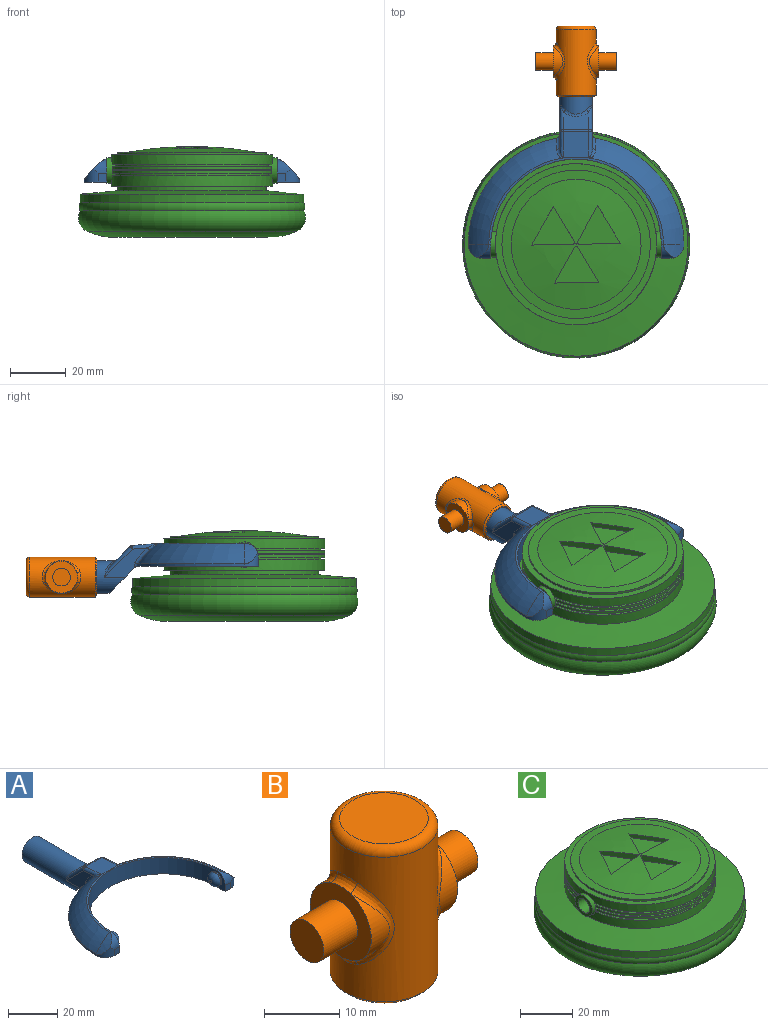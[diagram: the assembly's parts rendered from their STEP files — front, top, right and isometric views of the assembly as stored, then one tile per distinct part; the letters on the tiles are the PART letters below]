
ASSEMBLY  parts=3 mates=2
PART A: 48 faces, bbox 77.3x80.8x18.2 mm
  f0: plane 11.99x9.83mm, normal (0,-0.71,-0.71), area 141.5mm2, adj f1,f2,f9,f30,f43,f46
  f1: plane 15.39x10.49mm, normal (-1,0,0), area 63.5mm2, adj f0,f30,f32,f36,f46,f47
  f2: plane 15.39x10.49mm, normal (1,0,0), area 63.5mm2, adj f0,f30,f34,f39,f43,f44
  f3: plane 9.14x6.37mm, normal (0,0.71,0.71), area 67.6mm2, adj f35,f36,f39,f40
  f4: cylinder r=38.61mm len=37.99mm, axis (0,0,-1), area 42.6mm2, adj f6,f9,f17,f46,f47
  f5: torus R=19.3mm, axis (0,0,-1), area 507.8mm2, adj f10,f11,f12,f29,f42,f44
  f6: torus R=19.3mm, axis (0,0,-1), area 507.8mm2, adj f4,f11,f15,f28,f45,f47
  f7: cylinder r=30.48mm len=60.96mm, axis (0,0,-1), area 746.6mm2, adj f8,f9,f11,f14,f21,f24
  f8: plane 8.13x5.08mm, normal (-1,0,0), area 19.9mm2, adj f7,f9,f13,f19,f24
  f9: plane 77.22x43.73mm, normal (0,0,-1), area 956.2mm2, adj f0,f4,f7,f8,f10,f13,f14,f16
  f10: cylinder r=38.61mm len=37.99mm, axis (0,0,-1), area 42.6mm2, adj f5,f9,f20,f43,f44
  f11: plane 62.55x30.95mm, normal (0,0,1), area 75mm2, adj f5,f6,f7,f18,f19,f27
  f12: cylinder r=22.71mm len=7.33mm, axis (0,1,0), area 24.8mm2, adj f5,f19,f20
  f13: plane 3.05x3.05mm, normal (0,-1,0), area 9.3mm2, adj f8,f9,f19,f20
  f14: plane 8.13x5.08mm, normal (1,0,0), area 19.9mm2, adj f7,f9,f16,f18,f21
  f15: cylinder r=22.71mm len=7.33mm, axis (0,1,0), area 24.8mm2, adj f6,f17,f18
  f16: plane 3.05x3.05mm, normal (0,-1,0), area 9.3mm2, adj f9,f14,f17,f18
  f17: cylinder r=5.08mm len=5.08mm, axis (0,0,-1), area 21.9mm2, adj f4,f9,f15,f16,f18
  f18: cylinder r=5.08mm len=5.08mm, axis (-1,0,0), area 21.9mm2, adj f11,f14,f15,f16,f17
  f19: cylinder r=5.08mm len=5.08mm, axis (-1,0,0), area 21.9mm2, adj f8,f11,f12,f13,f20
  f20: cylinder r=5.08mm len=5.08mm, axis (0,0,-1), area 21.9mm2, adj f9,f10,f12,f13,f19
  f21: cylinder r=3.17mm len=6.35mm, axis (-1,0,0), area 12.7mm2, adj f7,f14,f23
  f22: plane 1.27x1.27mm, normal (1,0,0), area 1.3mm2, adj f23
  f23: torus R=0.64mm, axis (1,0,0), area 56.5mm2, adj f21,f22
  f24: cylinder r=3.17mm len=6.35mm, axis (1,0,0), area 12.7mm2, adj f7,f8,f26
  f25: plane 1.27x1.27mm, normal (-1,0,0), area 1.3mm2, adj f26
  f26: torus R=0.64mm, axis (-1,0,0), area 56.5mm2, adj f24,f25
  f27: plane 9.86x9.36mm, normal (0,0.09,1), area 85.6mm2, adj f11,f28,f29,f32,f34,f35,f42,f45
  f28: plane 1.04x0.17mm, normal (0,-1,0), area 0mm2, adj f6,f27,f45
  f29: plane 1.04x0.17mm, normal (0,-1,0), area 0mm2, adj f5,f27,f42
  f30: cylinder r=5.84mm len=33.01mm, axis (0,-1,0), area 1029.7mm2, adj f0,f1,f2,f31,f38,f40,f41
  f31: plane 11.68x11.68mm, normal (0,1,0), area 107.2mm2, adj f30
  f32: cylinder r=1.27mm len=9.13mm, axis (0,-1,0.09), area 14.4mm2, adj f1,f27,f33,f45
  f33: sphere r=1.27mm, area 1.5mm2, adj f32,f35,f36
  f34: cylinder r=1.27mm len=9.13mm, axis (0,1,-0.09), area 14.4mm2, adj f2,f27,f37,f42
  f35: cylinder r=1.27mm len=9.14mm, axis (-1,0,0), area 8.1mm2, adj f3,f27,f33,f37
  f36: cylinder r=1.27mm len=10.91mm, axis (0,-0.71,0.71), area 23.1mm2, adj f1,f3,f33,f38
  f37: sphere r=1.27mm, area 1.5mm2, adj f34,f35,f39
  f38: bspline ~4.55x2.75mm, area 2.3mm2, adj f30,f36,f40
  f39: cylinder r=1.27mm len=10.91mm, axis (0,0.71,-0.71), area 23.1mm2, adj f2,f3,f37,f41
  f40: bspline ~9.14x2.56mm, area 10.7mm2, adj f3,f30,f38,f41
  f41: bspline ~5.23x3.53mm, area 2.3mm2, adj f30,f39,f40
  f42: bspline ~4.62x3.14mm, area 5.2mm2, adj f5,f27,f29,f34,f44
  f43: cylinder r=1.27mm len=1.74mm, axis (0,0,-1), area 1.9mm2, adj f0,f2,f9,f10,f44
  f44: bspline ~8.6x7.86mm, area 11.9mm2, adj f2,f5,f10,f42,f43
  f45: bspline ~4.62x3.14mm, area 5.2mm2, adj f6,f27,f28,f32,f47
  f46: cylinder r=1.27mm len=1.74mm, axis (0,0,-1), area 1.9mm2, adj f0,f1,f4,f9,f47
  f47: bspline ~8.6x7.86mm, area 11.9mm2, adj f1,f4,f6,f45,f46
PART B: 25 faces, bbox 28.9x15.5x25.4 mm
  f0: cylinder r=5.71mm len=10.81mm, axis (-1,0,0), area 26.2mm2, adj f5,f15
  f1: cylinder r=5.71mm len=10.81mm, axis (-1,0,0), area 26.2mm2, adj f8,f11
  f2: cylinder r=7.14mm len=23.5mm, axis (0,0,-1), area 763.2mm2, adj f9,f10,f11,f12,f13,f14,f15,f16
  f3: plane 11.75x11.75mm, normal (0,0,1), area 108.4mm2, adj f17
  f4: plane 13.02x13.02mm, normal (0,0,-1), area 16.3mm2, adj f22,f24
  f5: plane 11.46x11.46mm, normal (1,0,0), area 70.9mm2, adj f0,f6,f13,f16,f18
  f6: cylinder r=5.71mm len=10.81mm, axis (-1,0,0), area 26.2mm2, adj f5,f14
  f7: cylinder r=5.71mm len=10.81mm, axis (-1,0,0), area 26.2mm2, adj f8,f10
  f8: plane 11.46x11.46mm, normal (-1,0,0), area 70.9mm2, adj f1,f7,f9,f12,f20
  f9: bspline ~4.64x1.73mm, area 6.5mm2, adj f2,f8,f10,f11
  f10: bspline ~13.62x4.91mm, area 20.7mm2, adj f2,f7,f9,f12
  f11: bspline ~13.6x4.87mm, area 20.7mm2, adj f1,f2,f9,f12
  f12: bspline ~4.64x1.73mm, area 6.5mm2, adj f2,f8,f10,f11
  f13: bspline ~4.64x1.73mm, area 6.5mm2, adj f2,f5,f14,f15
  f14: bspline ~13.62x4.91mm, area 20.7mm2, adj f2,f6,f13,f16
  f15: bspline ~13.6x4.87mm, area 20.7mm2, adj f0,f2,f13,f16
  f16: bspline ~4.64x1.73mm, area 6.5mm2, adj f2,f5,f14,f15
  f17: torus R=5.87mm, axis (0,0,1), area 83.8mm2, adj f2,f3
  f18: cylinder r=3.17mm len=6.35mm, axis (-1,0,0), area 126.7mm2, adj f5,f19
  f19: plane 6.35x6.35mm, normal (1,0,0), area 31.7mm2, adj f18
  f20: cylinder r=3.17mm len=6.35mm, axis (1,0,0), area 126.7mm2, adj f8,f21
  f21: plane 6.35x6.35mm, normal (-1,0,0), area 31.7mm2, adj f20
  f22: cylinder r=6.1mm len=22.86mm, axis (0,0,-1), area 875.6mm2, adj f4,f23
  f23: plane 12.19x12.19mm, normal (0,0,-1), area 116.7mm2, adj f22
  f24: cone r=7.14mm half-angle=45deg, axis (0,0,1), area 38.5mm2, adj f2,f4
PART C: 57 faces, bbox 96.3x96.3x32.5 mm
  f0: cylinder r=28.87mm len=57.73mm, axis (0,0,-1), area 676.7mm2, adj f1,f2,f33,f53,f54
  f1: plane 57.11x24.62mm, normal (0,0,1), area 101.3mm2, adj f0,f3,f53,f54
  f2: plane 57.11x24.62mm, normal (0,0,1), area 101.3mm2, adj f0,f4,f53,f54
  f3: cylinder r=27.6mm len=54.55mm, axis (0,0,-1), area 49.5mm2, adj f1,f6,f53,f54
  f4: cylinder r=27.6mm len=54.55mm, axis (0,0,-1), area 49.5mm2, adj f2,f5,f53,f54
  f5: plane 57.04x24.42mm, normal (0,0,-1), area 100.8mm2, adj f4,f8,f53,f54
  f6: plane 57.04x24.42mm, normal (0,0,-1), area 100.8mm2, adj f3,f7,f53,f54
  f7: cylinder r=28.87mm len=57.04mm, axis (0,0,-1), area 77.8mm2, adj f6,f10,f53,f54
  f8: cylinder r=28.87mm len=57.04mm, axis (0,0,-1), area 77.8mm2, adj f5,f9,f53,f54
  f9: plane 57.01x24.3mm, normal (0,0,1), area 100.5mm2, adj f8,f12,f53,f54
  f10: plane 57.01x24.3mm, normal (0,0,1), area 100.5mm2, adj f7,f11,f53,f54
  f11: cylinder r=27.6mm len=54.45mm, axis (0,0,-1), area 49.2mm2, adj f10,f14,f53,f54
  f12: cylinder r=27.6mm len=54.45mm, axis (0,0,-1), area 49.2mm2, adj f9,f13,f53,f54
  f13: plane 57.02x24.33mm, normal (0,0,-1), area 100.6mm2, adj f12,f16,f53,f54
  f14: plane 57.02x24.33mm, normal (0,0,-1), area 100.6mm2, adj f11,f15,f53,f54
  f15: cylinder r=28.87mm len=57.08mm, axis (0,0,-1), area 77.9mm2, adj f14,f18,f53,f54
  f16: cylinder r=28.87mm len=57.08mm, axis (0,0,-1), area 77.9mm2, adj f13,f17,f53,f54
  f17: plane 57.08x24.54mm, normal (0,0,1), area 101.1mm2, adj f16,f20,f53,f54
  f18: plane 57.08x24.54mm, normal (0,0,1), area 101.1mm2, adj f15,f19,f53,f54
  f19: cylinder r=27.6mm len=54.61mm, axis (0,0,-1), area 49.7mm2, adj f18,f21,f53,f54
  f20: cylinder r=27.6mm len=54.61mm, axis (0,0,-1), area 49.7mm2, adj f17,f22,f53,f54
  f21: plane 57.16x24.81mm, normal (0,0,-1), area 101.8mm2, adj f19,f23,f53,f54
  f22: plane 57.16x24.81mm, normal (0,0,-1), area 101.8mm2, adj f20,f23,f53,f54
  f23: cylinder r=28.87mm len=57.73mm, axis (0,0,-1), area 606.9mm2, adj f21,f22,f36,f53,f54
  f24: sphere r=135.39mm, area 1386mm2, adj f34,f37,f38,f39,f40,f42,f43,f44
  f25: plane 39.35x39.35mm, normal (0,0,-1), area 1216.2mm2, adj f26
  f26: torus R=20.13mm, axis (0,0,-1), area 1430.4mm2, adj f25,f27
  f27: torus R=27.75mm, axis (0,0,-1), area 3543.7mm2, adj f26,f28
  f28: torus R=35.37mm, axis (0,0,-1), area 2180.8mm2, adj f27,f29
  f29: torus R=37.36mm, axis (0,0,-1), area 734.8mm2, adj f28,f30
  f30: cylinder r=40.07mm len=80.14mm, axis (0,0,-1), area 799.3mm2, adj f29,f31
  f31: cone r=26.58mm half-angle=85deg, axis (0,0,-1), area 2834.9mm2, adj f30,f32
  f32: cylinder r=26.58mm len=53.16mm, axis (0,0,-1), area 265.1mm2, adj f31,f33
  f33: plane 57.73x57.73mm, normal (0,0,-1), area 398.2mm2, adj f0,f32
  f34: cone r=26.58mm half-angle=87deg, axis (0,0,-1), area 519.8mm2, adj f24,f35
  f35: cylinder r=26.58mm len=53.16mm, axis (0,0,-1), area 132.6mm2, adj f34,f36
  f36: plane 57.73x57.73mm, normal (0,0,1), area 398.2mm2, adj f23,f35
  f37: plane 15.1x2.54mm, normal (-0.02,1,0), area 33.4mm2, adj f24,f38,f40,f41
  f38: cylinder r=0.78mm len=2.54mm, axis (0,0,1), area 2.1mm2, adj f24,f37,f39,f41
  f39: plane 12.94x7.78mm, normal (-0.86,-0.51,0), area 33.4mm2, adj f24,f38,f40,f41
  f40: plane 13.88x7.7mm, normal (0.87,-0.48,0), area 28mm2, adj f24,f37,f39,f41
  f41: plane 15.47x13.88mm, normal (0,0,1), area 108.8mm2, adj f37,f38,f39,f40
  f42: plane 13.2x7.32mm, normal (0.87,-0.48,0), area 33.4mm2, adj f24,f43,f45,f46
  f43: cylinder r=0.78mm len=2.54mm, axis (0,0,1), area 2.1mm2, adj f24,f42,f44,f46
  f44: plane 15.1x2.54mm, normal (-0.02,1,0), area 33.4mm2, adj f24,f43,f45,f46
  f45: plane 13.61x8.18mm, normal (-0.86,-0.51,0), area 28mm2, adj f24,f42,f44,f46
  f46: plane 15.5x13.87mm, normal (0,0,1), area 108.8mm2, adj f42,f43,f44,f45
  f47: cylinder r=0.78mm len=2.54mm, axis (0,0,1), area 2.1mm2, adj f24,f48,f50,f51
  f48: plane 13.2x7.32mm, normal (0.87,-0.48,0), area 33.4mm2, adj f24,f47,f49,f51
  f49: plane 15.87x1.84mm, normal (-0.02,1,0), area 28mm2, adj f24,f48,f50,f51
  f50: plane 12.94x7.78mm, normal (-0.86,-0.51,0), area 33.4mm2, adj f24,f47,f49,f51
  f51: plane 15.87x13.22mm, normal (0,0,1), area 108.8mm2, adj f47,f48,f49,f50
  f52: plane 9.14x9.14mm, normal (1,0,0), area 34mm2, adj f53,f56
  f53: cylinder r=4.57mm len=9.14mm, axis (-1,0,0), area 56.6mm2, adj f0,f1,f2,f3,f4,f5,f6,f7
  f54: cylinder r=4.57mm len=9.14mm, axis (-1,0,0), area 56.6mm2, adj f0,f1,f2,f3,f4,f5,f6,f7
  f55: plane 9.14x9.14mm, normal (-1,0,0), area 34mm2, adj f54,f56
  f56: cylinder r=3.17mm len=60.96mm, axis (1,0,0), area 1216.1mm2, adj f52,f55
PLACE A t=(32.34,27.52,20.85)mm
PLACE B rot(axis=(-1,0,0),90deg) t=(32.34,80.3,16.88)mm
PLACE C t=(32.34,27.52,33.52)mm
MATE revolute A.f24 <-> C.f53  axis (-1,0,0) through (62.82,27.52,24.92)mm
MATE revolute B.f2 <-> A.f30  axis (0,-1,0) through (32.34,103.16,16.88)mm
